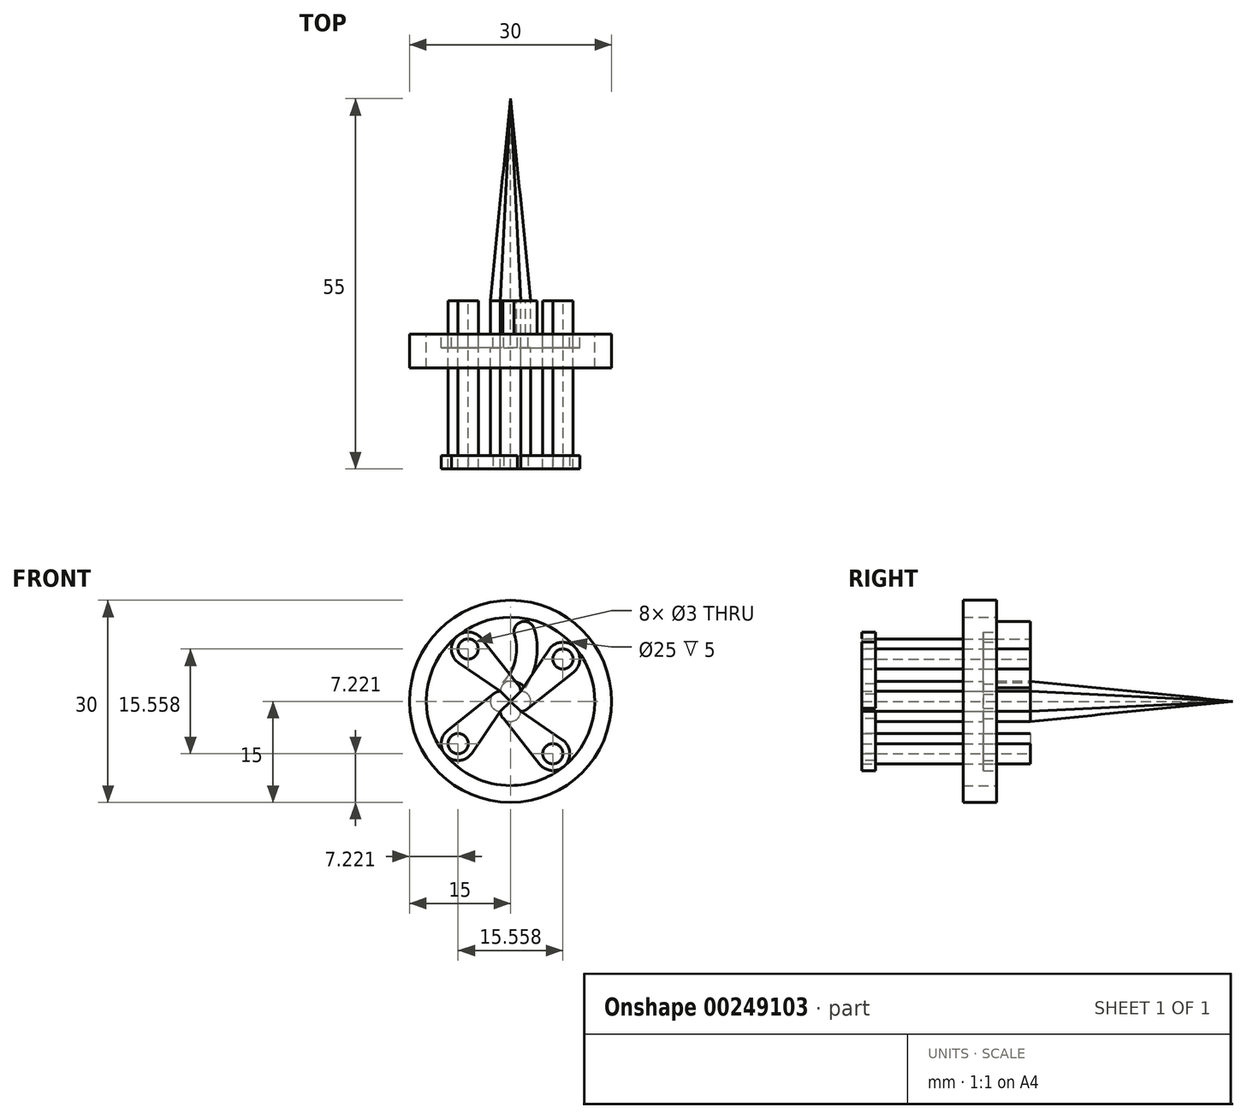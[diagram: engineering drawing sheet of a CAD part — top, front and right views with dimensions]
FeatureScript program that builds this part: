
annotation { "Feature Type Name" : "Feature", "Feature Type Description" : "" }
export const myFeature = defineFeature(function(context is Context, id is Id, definition is map)
    precondition{}
    {
        {
            var Q0;
            Q0=qCreatedBy(makeId("Front.planeOp"),FACE);
            var sketch = newSketch(context, id + "F0", { "sketchPlane" : qUnion([Q0])});
            skCircle(sketch, "E0", {"center": v(0, 0) * mm, "radius": 15 * mm, "construction": true});
            skLineSegment(sketch, "E1", {"start": v(0, 0) * mm, "end": v(0, 15) * mm, "construction": true});
            skCircle(sketch, "E2", {"center": v(0, 0) * mm, "radius": 10 * mm, "construction": true});
            skLineSegment(sketch, "E3", {"start": v(0, 0) * mm, "end": v(-1.5, 1.5) * mm});
            skLineSegment(sketch, "E4.MirrorCS", {"start": v(0, 0) * mm, "end": v(1.5, 1.5) * mm});
            skLineSegment(sketch, "E5.MirrorCS", {"start": v(0, 0) * mm, "end": v(15, 0) * mm, "construction": true});
            skLineSegment(sketch, "E6.MirrorCS", {"start": v(0, 0) * mm, "end": v(7.07, -7.07) * mm, "construction": true});
            skLineSegment(sketch, "E7.MirrorCS", {"start": v(0, 0) * mm, "end": v(-15, 0) * mm, "construction": true});
            skLineSegment(sketch, "E8.MirrorCS", {"start": v(0, 0) * mm, "end": v(-7.07, -7.07) * mm, "construction": true});
            skLineSegment(sketch, "E9.MirrorCS", {"start": v(0, 0) * mm, "end": v(0, -15) * mm, "construction": true});
            skArc(sketch, "E10", {"start": v(1.5, 1.5) * mm, "mid": v(0, 3) * mm, "end": v(-1.5, 1.5) * mm});
            skArc(sketch, "E11.1.0", {"start": v(0, -0.12) * mm, "mid": v(0, 0) * mm, "end": v(0, 0.12) * mm, "construction": true});
            skArc(sketch, "E11.2.0", {"start": v(0.12, 0) * mm, "mid": v(0, 0) * mm, "end": v(-0.12, 0) * mm, "construction": true});
            skArc(sketch, "E11.3.0", {"start": v(0, 0.12) * mm, "mid": v(0, 0) * mm, "end": v(0, -0.12) * mm, "construction": true});
            skArc(sketch, "E12.trimOffspring", {"start": v(1.5, -1.5) * mm, "mid": v(3, 0) * mm, "end": v(1.5, 1.5) * mm, "construction": true});
            skArc(sketch, "E13.trimOffspring", {"start": v(-1.5, -1.5) * mm, "mid": v(0, -3) * mm, "end": v(1.5, -1.5) * mm, "construction": true});
            skArc(sketch, "E14.trimOffspring", {"start": v(-0.12, 0) * mm, "mid": v(0, 0) * mm, "end": v(0.12, 0) * mm, "construction": true});
            skArc(sketch, "E15.trimOffspring", {"start": v(-1.5, 1.5) * mm, "mid": v(-3, 0) * mm, "end": v(-1.5, -1.5) * mm, "construction": true});
            skLineSegment(sketch, "E16", {"start": v(1.04, 2.58) * mm, "end": v(-5.03, 8.64) * mm});
            skLineSegment(sketch, "E17", {"start": v(0, 1.5) * mm, "end": v(-6.28, 7.78) * mm, "construction": true});
            skArc(sketch, "E18", {"start": v(0, 1.5) * mm, "mid": v(2.25, 5.3) * mm, "end": v(2.4, 9.71) * mm, "construction": true});
            skPoint(sketch, "E19.orphan", {"position": v(7.07, 7.07) * mm});
            skPoint(sketch, "E20.orphan", {"position": v(-7.07, 7.07) * mm});
            skLineSegment(sketch, "E21", {"start": v(-1.5, 1.5) * mm, "end": v(-7.07, 7.07) * mm});
            skSolve(sketch);
        }
        {
            var Q0;
            {var subQ0=sQuery(id+"F0.wireOp",EDGE,"E3");Q0=makeQuery(id+"F0.imprint","IMPRINT",FACE,{"disambiguationData":[TD([[makeQuery(id+"F0.imprint","IMPRINT",EDGE,{"derivedFrom":subQ0}),-1.0]])]});}
            extrude(context, id + "F1", {"entities" : qUnion([Q0]), "depth" : 25 * mm});
        }
        {
            var Q0;
            Q0=qCreatedBy(makeId("Front.planeOp"),FACE);
            cPlane(context, id + "F2", {"entities" : qUnion([Q0]), "cplaneType" : CPlaneType.OFFSET, "offset" : 30 * mm, "oppositeDirection" : true, "width" : 150 * mm, "height" : 150 * mm});
        }
        {
            var Q0;
            Q0=qCreatedBy(id+"F2.planeOp",FACE);
            var sketch = newSketch(context, id + "F3", { "sketchPlane" : qUnion([Q0])});
            skPoint(sketch, "E22", {"position": v(0, 0) * mm});
            skSolve(sketch);
        }
        {
            var Q1;
            {var subQ0=sQuery(id+"F0.wireOp",EDGE,"E3");Q1=makeQuery(id+"F0.imprint","IMPRINT",FACE,{"disambiguationData":[TD([[makeQuery(id+"F0.imprint","IMPRINT",EDGE,{"derivedFrom":subQ0}),-1.0]])]});}
            var Q2;
            Q2=sQuery(id+"F3.wireOp",VERTEX,"E22");
            loft(context, id + "F4", {"operationType" : NewBodyOperationType.ADD, "sheetProfilesArray" : [{ "sheetProfileEntities" : qUnion([Q1]) }, { "sheetProfileEntities" : qUnion([Q2]) }]});
        }
        {
            var Q0;
            Q0=qCreatedBy(makeId("Front.planeOp"),FACE);
            cPlane(context, id + "F5", {"entities" : qUnion([Q0]), "cplaneType" : CPlaneType.OFFSET, "offset" : 5 * mm, "width" : 150 * mm, "height" : 150 * mm});
        }
        {
            var Q0;
            Q0=qCreatedBy(id+"F5.planeOp",FACE);
            var sketch = newSketch(context, id + "F6", { "sketchPlane" : qUnion([Q0])});
            skArc(sketch, "E23.0", {"start": v(1.04, 2.58) * mm, "mid": v(-0.59, 2.88) * mm, "end": v(-1.5, 1.5) * mm});
            skPoint(sketch, "E24.orphan", {"position": v(1.5, 1.5) * mm});
            skPoint(sketch, "E25.0", {"position": v(-6.28, 7.78) * mm});
            skCircle(sketch, "E26", {"center": v(-6.28, 7.78) * mm, "radius": 1.5 * mm});
            skArc(sketch, "E27", {"start": v(-4.33, 9.33) * mm, "mid": v(-8.12, 9.48) * mm, "end": v(-7.7, 5.71) * mm});
            skLineSegment(sketch, "E28", {"start": v(1.04, 2.58) * mm, "end": v(-4.33, 9.33) * mm});
            skLineSegment(sketch, "E29", {"start": v(-1.5, 1.5) * mm, "end": v(-7.7, 5.71) * mm});
            skSolve(sketch);
        }
        {
            var Q0;
            Q0=makeQuery(id+"F6.imprint","IMPRINT",FACE,{"disambiguationData":[TD([[makeQuery(id+"F6.imprint","IMPRINT",EDGE,{"derivedFrom":sQuery(id+"F6.wireOp",EDGE,"E23.0")}),-1.0]])]});
            extrude(context, id + "F7", {"entities" : qUnion([Q0]), "operationType" : NewBodyOperationType.ADD, "depth" : 2 * mm});
        }
        {
            var Q0;
            Q0=makeQuery(id+"F1.opExtrude","CAP_FACE",FACE,{"disambiguationData":[OSD([sQuery(id+"F0.wireOp",EDGE,"E3"),sQuery(id+"F0.wireOp",EDGE,"E4.MirrorCS"),sQuery(id+"F0.wireOp",EDGE,"E10")])],"isStart":false});
            var sketch = newSketch(context, id + "F8", { "sketchPlane" : qUnion([Q0])});
            skCircle(sketch, "E30.0", {"center": v(-6.28, 7.78) * mm, "radius": 1.5 * mm});
            skArc(sketch, "E31.0", {"start": v(-4.33, 9.33) * mm, "mid": v(-8.12, 9.48) * mm, "end": v(-7.7, 5.71) * mm});
            skLineSegment(sketch, "E32.0", {"start": v(1.04, 2.58) * mm, "end": v(-4.33, 9.33) * mm});
            skLineSegment(sketch, "E33.0", {"start": v(-1.5, 1.5) * mm, "end": v(-7.7, 5.71) * mm});
            skArc(sketch, "E34.0", {"start": v(1.04, 2.58) * mm, "mid": v(-0.59, 2.88) * mm, "end": v(-1.5, 1.5) * mm});
            skPoint(sketch, "E35.orphan", {"position": v(1.5, 1.5) * mm});
            skSolve(sketch);
        }
        {
            var Q0;
            Q0=makeQuery(id+"F8.imprint","IMPRINT",FACE,{"disambiguationData":[TD([[makeQuery(id+"F8.imprint","IMPRINT",EDGE,{"derivedFrom":sQuery(id+"F8.wireOp",EDGE,"E30.0")}),-1.0]])]});
            extrude(context, id + "F9", {"entities" : qUnion([Q0]), "operationType" : NewBodyOperationType.ADD, "oppositeDirection" : true, "depth" : 2 * mm});
        }
        {
            var Q0;
            Q0=makeQuery(id+"F1.opExtrude","SWEPT_BODY",BODY,{"disambiguationData":[OSD([sQuery(id+"F0.wireOp",EDGE,"E3"),sQuery(id+"F0.wireOp",EDGE,"E4.MirrorCS"),sQuery(id+"F0.wireOp",EDGE,"E10")])]});
            var Q1;
            {var subQ0=sQuery(id+"F0.wireOp",EDGE,"E4.MirrorCS");var subQ1=sQuery(id+"F0.wireOp",EDGE,"E3");Q1=makeQuery(id+"F4.boolean.opBoolean","MERGE",EDGE,{"derivedFrom":[makeQuery(id+"F1.opExtrude","SWEPT_EDGE",EDGE,{"disambiguationData":[OSD([subQ1,subQ0])]}),makeQuery(id+"F4.opLoft","SWEPT_EDGE",EDGE,{"disambiguationData":[OSD([subQ1,subQ0,sQuery(id+"F3.wireOp",VERTEX,"E22")])]})]});}
            circularPattern(context, id + "F10", {"entities" : qUnion([Q0]), "axis" : qUnion([Q1]), "angle" : 360 * degree, "instanceCount" : 4, "equalSpace" : true});
        }
        {
            var Q0;
            Q0=qCreatedBy(makeId("Front.planeOp"),FACE);
            var sketch = newSketch(context, id + "F11", { "sketchPlane" : qUnion([Q0])});
            skCircle(sketch, "E36.0", {"center": v(0, 0) * mm, "radius": 15 * mm});
            skCircle(sketch, "E37.0", {"center": v(7.78, 6.28) * mm, "radius": 1.5 * mm});
            skArc(sketch, "E38.0", {"start": v(1.5, 1.5) * mm, "mid": v(0, 3) * mm, "end": v(-1.5, 1.5) * mm, "construction": true});
            skCircle(sketch, "E39", {"center": v(0, 0) * mm, "radius": 3 * mm});
            skCircle(sketch, "E40.0", {"center": v(-6.28, 7.78) * mm, "radius": 1.5 * mm});
            skCircle(sketch, "E41.0", {"center": v(-7.78, -6.28) * mm, "radius": 1.5 * mm});
            skCircle(sketch, "E42.0", {"center": v(6.28, -7.78) * mm, "radius": 1.5 * mm});
            skSolve(sketch);
        }
        {
            var Q0;
            Q0=makeQuery(id+"F11.imprint","IMPRINT",FACE,{"disambiguationData":[TD([[makeQuery(id+"F11.imprint","IMPRINT",EDGE,{"derivedFrom":sQuery(id+"F11.wireOp",EDGE,"E36.0")}),1.0]])]});
            extrude(context, id + "F12", {"entities" : qUnion([Q0]), "depth" : 5 * mm});
        }
        {
            var Q0;
            Q0=makeQuery(id+"F12.opExtrude","CAP_FACE",FACE,{"disambiguationData":[OSD([sQuery(id+"F11.wireOp",EDGE,"E36.0"),sQuery(id+"F11.wireOp",EDGE,"E37.0"),sQuery(id+"F11.wireOp",EDGE,"E39"),sQuery(id+"F11.wireOp",EDGE,"E40.0"),sQuery(id+"F11.wireOp",EDGE,"E41.0"),sQuery(id+"F11.wireOp",EDGE,"E42.0")])],"isStart":true});
            var sketch = newSketch(context, id + "F13", { "sketchPlane" : qUnion([Q0])});
            skArc(sketch, "E43.0", {"start": v(0, 1.5) * mm, "mid": v(-2.25, 5.3) * mm, "end": v(-2.4, 9.71) * mm, "construction": true});
            skPoint(sketch, "E44.0", {"position": v(-1.5, 1.5) * mm});
            skArc(sketch, "E45", {"start": v(-1.5, 1.5) * mm, "mid": v(-3.54, 5.89) * mm, "end": v(-3.27, 10.72) * mm, "construction": true});
            skArc(sketch, "E46.0", {"start": v(-1.5, 1.5) * mm, "mid": v(0, 3) * mm, "end": v(1.5, 1.5) * mm, "construction": true});
            skArc(sketch, "E47", {"start": v(0.79, 2.77) * mm, "mid": v(-0.97, 6.16) * mm, "end": v(-0.82, 9.97) * mm, "construction": true});
            skCircle(sketch, "E48.0", {"center": v(0, 0) * mm, "radius": 10 * mm, "construction": true});
            skArc(sketch, "E49", {"start": v(-0.82, 9.97) * mm, "mid": v(-1.67, 11.57) * mm, "end": v(-3.27, 10.72) * mm, "construction": true});
            skArc(sketch, "E50.0", {"start": v(-2.2, 2.03) * mm, "mid": v(-3.85, 6.27) * mm, "end": v(-3.51, 10.8) * mm});
            skArc(sketch, "E51.0", {"start": v(1.12, 2.78) * mm, "mid": v(-0.7, 6.1) * mm, "end": v(-0.58, 9.9) * mm});
            skArc(sketch, "E52", {"start": v(-0.58, 9.9) * mm, "mid": v(-1.6, 11.8) * mm, "end": v(-3.51, 10.8) * mm});
            skArc(sketch, "E53.0", {"start": v(1.12, 2.78) * mm, "mid": v(-0.66, 2.93) * mm, "end": v(-2.2, 2.03) * mm});
            skArc(sketch, "E54.1.0", {"start": v(-9.9, -0.58) * mm, "mid": v(-11.8, -1.6) * mm, "end": v(-10.8, -3.51) * mm});
            skArc(sketch, "E54.1.1", {"start": v(-2.03, -2.2) * mm, "mid": v(-6.27, -3.85) * mm, "end": v(-10.8, -3.51) * mm});
            skArc(sketch, "E54.1.2", {"start": v(-2.78, 1.12) * mm, "mid": v(-6.1, -0.7) * mm, "end": v(-9.9, -0.58) * mm});
            skArc(sketch, "E54.1.3", {"start": v(-2.78, 1.12) * mm, "mid": v(-2.93, -0.66) * mm, "end": v(-2.03, -2.2) * mm});
            skArc(sketch, "E54.2.0", {"start": v(0.58, -9.9) * mm, "mid": v(1.6, -11.8) * mm, "end": v(3.51, -10.8) * mm});
            skArc(sketch, "E54.2.1", {"start": v(2.2, -2.03) * mm, "mid": v(3.85, -6.27) * mm, "end": v(3.51, -10.8) * mm});
            skArc(sketch, "E54.2.2", {"start": v(-1.12, -2.78) * mm, "mid": v(0.7, -6.1) * mm, "end": v(0.58, -9.9) * mm});
            skArc(sketch, "E54.2.3", {"start": v(-1.12, -2.78) * mm, "mid": v(0.66, -2.93) * mm, "end": v(2.2, -2.03) * mm});
            skArc(sketch, "E54.3.0", {"start": v(9.9, 0.58) * mm, "mid": v(11.8, 1.6) * mm, "end": v(10.8, 3.51) * mm});
            skArc(sketch, "E54.3.1", {"start": v(2.03, 2.2) * mm, "mid": v(6.27, 3.85) * mm, "end": v(10.8, 3.51) * mm});
            skArc(sketch, "E54.3.2", {"start": v(2.78, -1.12) * mm, "mid": v(6.1, 0.7) * mm, "end": v(9.9, 0.58) * mm});
            skArc(sketch, "E54.3.3", {"start": v(2.78, -1.12) * mm, "mid": v(2.93, 0.66) * mm, "end": v(2.03, 2.2) * mm});
            skSolve(sketch);
        }
        {
            var Q0;
            Q0=makeQuery(id+"F13.imprint","IMPRINT",FACE,{"disambiguationData":[TD([[makeQuery(id+"F13.imprint","IMPRINT",EDGE,{"derivedFrom":sQuery(id+"F13.wireOp",EDGE,"E50.0")}),-1.0]])]});
            var Q1;
            Q1=makeQuery(id+"F13.imprint","IMPRINT",FACE,{"disambiguationData":[TD([[makeQuery(id+"F13.imprint","IMPRINT",EDGE,{"derivedFrom":sQuery(id+"F13.wireOp",EDGE,"E54.1.0")}),1.0]])]});
            var Q2;
            Q2=makeQuery(id+"F13.imprint","IMPRINT",FACE,{"disambiguationData":[TD([[makeQuery(id+"F13.imprint","IMPRINT",EDGE,{"derivedFrom":sQuery(id+"F13.wireOp",EDGE,"E54.3.0")}),1.0]])]});
            var Q3;
            Q3=makeQuery(id+"F13.imprint","IMPRINT",FACE,{"disambiguationData":[TD([[makeQuery(id+"F13.imprint","IMPRINT",EDGE,{"derivedFrom":sQuery(id+"F13.wireOp",EDGE,"E54.2.0")}),1.0]])]});
            extrude(context, id + "F14", {"entities" : qUnion([Q0, Q1, Q2, Q3]), "operationType" : NewBodyOperationType.REMOVE, "oppositeDirection" : true, "depth" : 5 * mm});
        }
        {
            var Q0;
            Q0=makeQuery(id+"F12.opExtrude","CAP_FACE",FACE,{"disambiguationData":[OSD([sQuery(id+"F11.wireOp",EDGE,"E36.0"),sQuery(id+"F11.wireOp",EDGE,"E37.0"),sQuery(id+"F11.wireOp",EDGE,"E39"),sQuery(id+"F11.wireOp",EDGE,"E40.0"),sQuery(id+"F11.wireOp",EDGE,"E41.0"),sQuery(id+"F11.wireOp",EDGE,"E42.0")])],"isStart":false});
            var sketch = newSketch(context, id + "F15", { "sketchPlane" : qUnion([Q0])});
            skCircle(sketch, "E55.0", {"center": v(0, 0) * mm, "radius": 15 * mm});
            skPoint(sketch, "E56.0", {"position": v(9.48, 8.12) * mm});
            skCircle(sketch, "E57", {"center": v(0, 0) * mm, "radius": 12.5 * mm});
            skSolve(sketch);
        }
        {
            var Q0;
            Q0=makeQuery(id+"F15.imprint","IMPRINT",FACE,{"disambiguationData":[TD([[makeQuery(id+"F15.imprint","IMPRINT",EDGE,{"derivedFrom":sQuery(id+"F15.wireOp",EDGE,"E57")}),-1.0]])]});
            var Q1;
            Q1=makeQuery(id+"F10.opPattern","COPY",FACE,{"derivedFrom":makeQuery(id+"F9.boolean.opBoolean","MERGE",FACE,{"derivedFrom":[makeQuery(id+"F1.opExtrude","CAP_FACE",FACE,{"disambiguationData":[OSD([sQuery(id+"F0.wireOp",EDGE,"E3"),sQuery(id+"F0.wireOp",EDGE,"E4.MirrorCS"),sQuery(id+"F0.wireOp",EDGE,"E10")])],"isStart":false}),makeQuery(id+"F9.opExtrude","CAP_FACE",FACE,{"disambiguationData":[OSD([sQuery(id+"F8.wireOp",EDGE,"E30.0"),sQuery(id+"F8.wireOp",EDGE,"E31.0"),sQuery(id+"F8.wireOp",EDGE,"E32.0"),sQuery(id+"F8.wireOp",EDGE,"E33.0"),sQuery(id+"F8.wireOp",EDGE,"E34.0")])],"isStart":true})]}),"instanceName":"2"});
            extrude(context, id + "F16", {"entities" : qUnion([Q0]), "endBoundEntityFace" : qUnion([Q1]), "depth" : 5 * mm});
        }
        {
            var Q0;
            Q0=makeQuery(id+"F12.opExtrude","CAP_FACE",FACE,{"disambiguationData":[OSD([sQuery(id+"F11.wireOp",EDGE,"E36.0"),sQuery(id+"F11.wireOp",EDGE,"E37.0"),sQuery(id+"F11.wireOp",EDGE,"E39"),sQuery(id+"F11.wireOp",EDGE,"E40.0"),sQuery(id+"F11.wireOp",EDGE,"E41.0"),sQuery(id+"F11.wireOp",EDGE,"E42.0")])],"isStart":true});
            var sketch = newSketch(context, id + "F17", { "sketchPlane" : qUnion([Q0])});
            skCircle(sketch, "E58.0", {"center": v(6.28, 7.78) * mm, "radius": 1.5 * mm});
            skCircle(sketch, "E59.0", {"center": v(-7.78, 6.28) * mm, "radius": 1.5 * mm});
            skCircle(sketch, "E60.0", {"center": v(-6.28, -7.78) * mm, "radius": 1.5 * mm});
            skCircle(sketch, "E61.0", {"center": v(7.78, -6.28) * mm, "radius": 1.5 * mm});
            skSolve(sketch);
        }
        {
            var Q0;
            Q0 = qSketchRegion(id + "F17", true);
            extrude(context, id + "F18", {"entities" : qUnion([Q0]), "oppositeDirection" : true, "depth" : 25 * mm});
        }
    });
